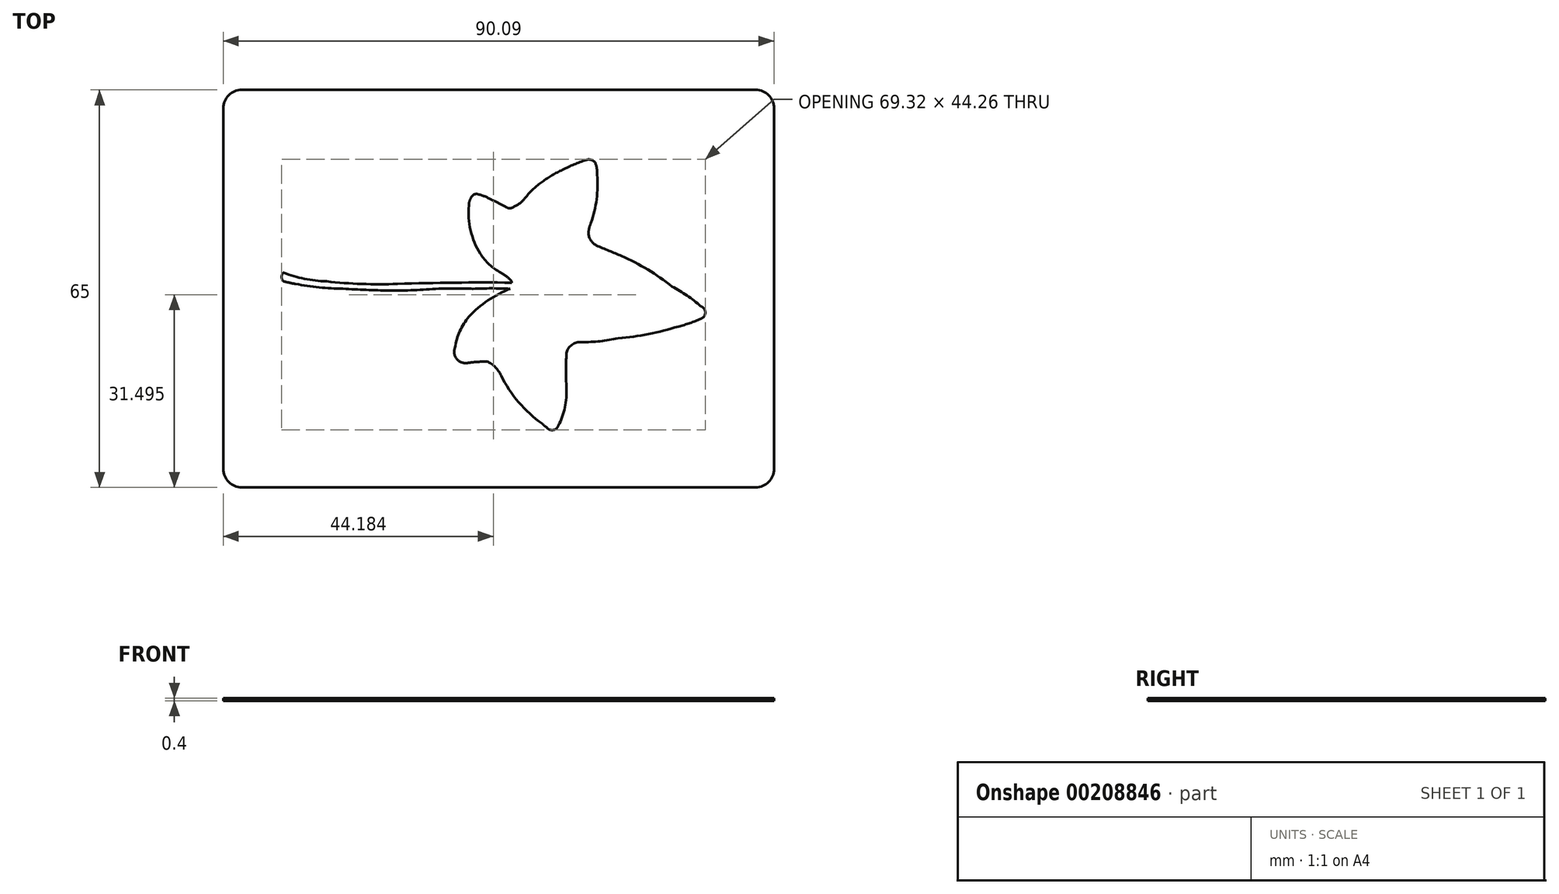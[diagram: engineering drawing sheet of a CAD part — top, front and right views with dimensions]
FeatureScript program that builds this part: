
annotation { "Feature Type Name" : "Feature", "Feature Type Description" : "" }
export const myFeature = defineFeature(function(context is Context, id is Id, definition is map)
    precondition{}
    {
        {
            var Q0;
            Q0=qCreatedBy(makeId("Top.planeOp"),FACE);
            var sketch = newSketch(context, id + "F0", { "sketchPlane" : qUnion([Q0])});
            skLineSegment(sketch, "E0.bottom", {"start": v(-79.56, 38.56) * mm, "end": v(10.53, 38.56) * mm});
            skLineSegment(sketch, "E0.top", {"start": v(-79.56, 103.56) * mm, "end": v(10.53, 103.56) * mm});
            skArc(sketch, "E1", {"start": v(-69.73, 73.68) * mm, "mid": v(-66.28, 72.66) * mm, "end": v(-62.7, 72.25) * mm});
            skArc(sketch, "E2", {"start": v(-62.7, 72.25) * mm, "mid": v(-56.9, 71.83) * mm, "end": v(-51.08, 71.83) * mm});
            skArc(sketch, "E3", {"start": v(-32.39, 72.03) * mm, "mid": v(-41.74, 72.04) * mm, "end": v(-51.08, 71.83) * mm});
            skArc(sketch, "E4", {"start": v(-69.73, 72.25) * mm, "mid": v(-68.75, 72.02) * mm, "end": v(-67.76, 71.83) * mm});
            skArc(sketch, "E5", {"start": v(-67.76, 71.83) * mm, "mid": v(-63.88, 71.26) * mm, "end": v(-59.98, 71.06) * mm});
            skArc(sketch, "E6", {"start": v(-59.98, 71.06) * mm, "mid": v(-56.2, 70.85) * mm, "end": v(-52.41, 70.74) * mm});
            skArc(sketch, "E7", {"start": v(-52.41, 70.74) * mm, "mid": v(-48.37, 70.8) * mm, "end": v(-44.33, 71.06) * mm});
            skArc(sketch, "E8", {"start": v(-38.71, 71.04) * mm, "mid": v(-41.52, 71.06) * mm, "end": v(-44.33, 71.06) * mm});
            skArc(sketch, "E9", {"start": v(-69.73, 73.68) * mm, "mid": v(-70.04, 72.97) * mm, "end": v(-69.73, 72.25) * mm});
            skArc(sketch, "E10", {"start": v(-32.62, 71.04) * mm, "mid": v(-35.67, 71.1) * mm, "end": v(-38.71, 71.04) * mm});
            skArc(sketch, "E11", {"start": v(-32.62, 71.04) * mm, "mid": v(-36.26, 69.13) * mm, "end": v(-39.4, 66.47) * mm});
            skArc(sketch, "E12", {"start": v(-39.4, 66.47) * mm, "mid": v(-40.87, 64.1) * mm, "end": v(-41.67, 61.41) * mm});
            skArc(sketch, "E13", {"start": v(-41.67, 61.41) * mm, "mid": v(-41.3, 59.48) * mm, "end": v(-39.4, 58.94) * mm});
            skArc(sketch, "E14", {"start": v(-36.41, 59.15) * mm, "mid": v(-37.9, 59.08) * mm, "end": v(-39.4, 58.94) * mm});
            skArc(sketch, "E15", {"start": v(-34.11, 56.83) * mm, "mid": v(-35.05, 58.2) * mm, "end": v(-36.41, 59.15) * mm});
            skArc(sketch, "E16", {"start": v(-34.11, 56.83) * mm, "mid": v(-31.24, 52.47) * mm, "end": v(-27.38, 48.96) * mm});
            skArc(sketch, "E17", {"start": v(-27.38, 48.96) * mm, "mid": v(-27.05, 48.64) * mm, "end": v(-26.67, 48.38) * mm});
            skArc(sketch, "E18", {"start": v(-26.67, 48.38) * mm, "mid": v(-25.63, 47.93) * mm, "end": v(-24.76, 48.64) * mm});
            skArc(sketch, "E19", {"start": v(-24.76, 48.64) * mm, "mid": v(-23.67, 51.64) * mm, "end": v(-23.44, 54.81) * mm});
            skArc(sketch, "E20", {"start": v(-23.44, 60.5) * mm, "mid": v(-23.48, 57.65) * mm, "end": v(-23.44, 54.81) * mm});
            skArc(sketch, "E21", {"start": v(-20.91, 62.32) * mm, "mid": v(-22.52, 61.88) * mm, "end": v(-23.44, 60.5) * mm});
            skArc(sketch, "E22", {"start": v(-20.91, 62.32) * mm, "mid": v(-17.93, 62.45) * mm, "end": v(-14.98, 62.94) * mm});
            skArc(sketch, "E23", {"start": v(-14.98, 62.94) * mm, "mid": v(-9.98, 63.63) * mm, "end": v(-5.08, 64.87) * mm});
            skArc(sketch, "E24", {"start": v(-5.08, 64.87) * mm, "mid": v(-3.23, 65.42) * mm, "end": v(-1.43, 66.13) * mm});
            skArc(sketch, "E25", {"start": v(-1.43, 66.13) * mm, "mid": v(-0.71, 67.15) * mm, "end": v(-1.43, 68.16) * mm});
            skArc(sketch, "E26", {"start": v(-1.43, 68.16) * mm, "mid": v(-3.7, 69.92) * mm, "end": v(-6.15, 71.4) * mm});
            skArc(sketch, "E27", {"start": v(-6.15, 71.4) * mm, "mid": v(-10.12, 74.17) * mm, "end": v(-14.4, 76.41) * mm});
            skArc(sketch, "E28", {"start": v(-19.42, 81.81) * mm, "mid": v(-18.5, 85.68) * mm, "end": v(-18.4, 89.67) * mm});
            skArc(sketch, "E29", {"start": v(-19.8, 80.44) * mm, "mid": v(-19.52, 79.08) * mm, "end": v(-18.53, 78.13) * mm});
            skArc(sketch, "E30", {"start": v(-18.4, 89.67) * mm, "mid": v(-18.45, 90.7) * mm, "end": v(-18.75, 91.68) * mm});
            skArc(sketch, "E31", {"start": v(-18.53, 78.13) * mm, "mid": v(-16.47, 77.25) * mm, "end": v(-14.4, 76.41) * mm});
            skArc(sketch, "E32", {"start": v(-33.52, 84.53) * mm, "mid": v(-32.71, 84.22) * mm, "end": v(-31.91, 84.53) * mm});
            skArc(sketch, "E33", {"start": v(-37.88, 86.5) * mm, "mid": v(-38.6, 86.43) * mm, "end": v(-39.06, 85.87) * mm});
            skArc(sketch, "E34", {"start": v(-39.4, 84.67) * mm, "mid": v(-39.1, 80.57) * mm, "end": v(-37.53, 76.77) * mm});
            skArc(sketch, "E35", {"start": v(-37.53, 76.77) * mm, "mid": v(-36.05, 75.01) * mm, "end": v(-34.18, 73.68) * mm});
            skArc(sketch, "E36", {"start": v(-27.35, 88.53) * mm, "mid": v(-28.82, 87.39) * mm, "end": v(-30.08, 86.02) * mm});
            skArc(sketch, "E37", {"start": v(-31.91, 84.53) * mm, "mid": v(-30.9, 85.14) * mm, "end": v(-30.08, 86.02) * mm});
            skArc(sketch, "E38", {"start": v(-35.53, 85.5) * mm, "mid": v(-36.67, 86.09) * mm, "end": v(-37.88, 86.5) * mm});
            skArc(sketch, "E39", {"start": v(-33.52, 84.53) * mm, "mid": v(-34.51, 85.04) * mm, "end": v(-35.53, 85.5) * mm});
            skArc(sketch, "E40", {"start": v(-39.06, 85.87) * mm, "mid": v(-39.3, 85.3) * mm, "end": v(-39.4, 84.67) * mm});
            skArc(sketch, "E41", {"start": v(-18.75, 91.68) * mm, "mid": v(-19.42, 92.14) * mm, "end": v(-20.22, 92.1) * mm});
            skArc(sketch, "E42", {"start": v(-20.22, 92.1) * mm, "mid": v(-22.17, 91.37) * mm, "end": v(-24.05, 90.49) * mm});
            skArc(sketch, "E43", {"start": v(-24.05, 90.49) * mm, "mid": v(-25.76, 89.61) * mm, "end": v(-27.35, 88.53) * mm});
            skArc(sketch, "E44", {"start": v(-32.39, 72.03) * mm, "mid": v(-32.45, 72.32) * mm, "end": v(-32.65, 72.54) * mm});
            skArc(sketch, "E45", {"start": v(-32.65, 72.54) * mm, "mid": v(-33.37, 73.17) * mm, "end": v(-34.18, 73.68) * mm});
            skArc(sketch, "E46", {"start": v(-19.42, 81.81) * mm, "mid": v(-19.66, 81.14) * mm, "end": v(-19.8, 80.44) * mm});
            skLineSegment(sketch, "E47", {"start": v(-79.56, 38.56) * mm, "end": v(-79.56, 103.56) * mm});
            skLineSegment(sketch, "E48", {"start": v(10.53, 103.56) * mm, "end": v(10.53, 38.56) * mm});
            skSolve(sketch);
        }
        {
            var Q0;
            Q0=makeQuery(id+"F0.imprint","IMPRINT",FACE,{"disambiguationData":[TD([[makeQuery(id+"F0.imprint","IMPRINT",EDGE,{"derivedFrom":sQuery(id+"F0.wireOp",EDGE,"E0.bottom")}),1.0]])]});
            extrude(context, id + "F1", {"entities" : qUnion([Q0]), "depth" : 0.4 * mm});
        }
        {
            var Q0;
            Q0=makeQuery(id+"F1.opExtrude","SWEPT_EDGE",EDGE,{"disambiguationData":[OSD([sQuery(id+"F0.wireOp",EDGE,"E0.bottom"),sQuery(id+"F0.wireOp",EDGE,"E47")])]});
            var Q1;
            Q1=makeQuery(id+"F1.opExtrude","SWEPT_EDGE",EDGE,{"disambiguationData":[OSD([sQuery(id+"F0.wireOp",EDGE,"E0.top"),sQuery(id+"F0.wireOp",EDGE,"E47")])]});
            var Q2;
            Q2=makeQuery(id+"F1.opExtrude","SWEPT_EDGE",EDGE,{"disambiguationData":[OSD([sQuery(id+"F0.wireOp",EDGE,"E0.bottom"),sQuery(id+"F0.wireOp",EDGE,"E48")])]});
            var Q3;
            Q3=makeQuery(id+"F1.opExtrude","SWEPT_EDGE",EDGE,{"disambiguationData":[OSD([sQuery(id+"F0.wireOp",EDGE,"E0.top"),sQuery(id+"F0.wireOp",EDGE,"E48")])]});
            fillet(context, id + "F2", {"entities" : qUnion([Q0, Q1, Q2, Q3]), "radius" : 3 * mm, "tangentPropagation" : true, "allowEdgeOverflow" : false});
        }
    });
